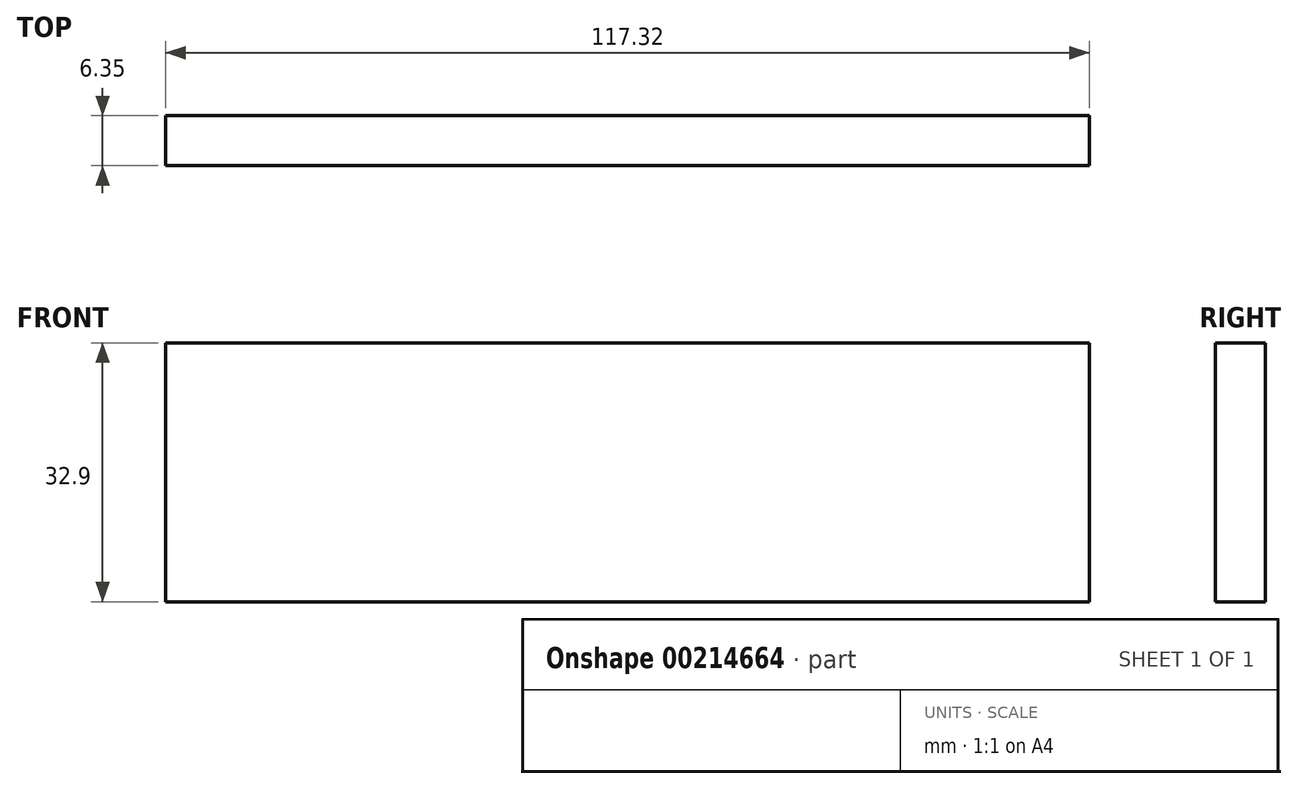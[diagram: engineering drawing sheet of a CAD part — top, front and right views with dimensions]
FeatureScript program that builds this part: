
annotation { "Feature Type Name" : "Feature", "Feature Type Description" : "" }
export const myFeature = defineFeature(function(context is Context, id is Id, definition is map)
    precondition{}
    {
        {
            var Q0;
            Q0=qCreatedBy(makeId("Front.planeOp"),FACE);
            var sketch = newSketch(context, id + "F0", { "sketchPlane" : qUnion([Q0])});
            skLineSegment(sketch, "E0.bottom", {"start": v(-58.66, -16.45) * mm, "end": v(58.66, -16.45) * mm});
            skLineSegment(sketch, "E0.top", {"start": v(-58.66, 16.45) * mm, "end": v(58.66, 16.45) * mm});
            skLineSegment(sketch, "E0.left", {"start": v(-58.66, -16.45) * mm, "end": v(-58.66, 16.45) * mm});
            skLineSegment(sketch, "E0.right", {"start": v(58.66, -16.45) * mm, "end": v(58.66, 16.45) * mm});
            skPoint(sketch, "E0.middle", {"position": v(0, 0) * mm});
            skSolve(sketch);
        }
        {
            var Q0;
            Q0=makeQuery(id+"F0.imprint","IMPRINT",FACE,{"disambiguationData":[TD([[makeQuery(id+"F0.imprint","IMPRINT",EDGE,{"derivedFrom":sQuery(id+"F0.wireOp",EDGE,"E0.bottom")}),1.0]])]});
            extrude(context, id + "F1", {"entities" : qUnion([Q0]), "depth" : 6.35 * mm});
        }
    });
